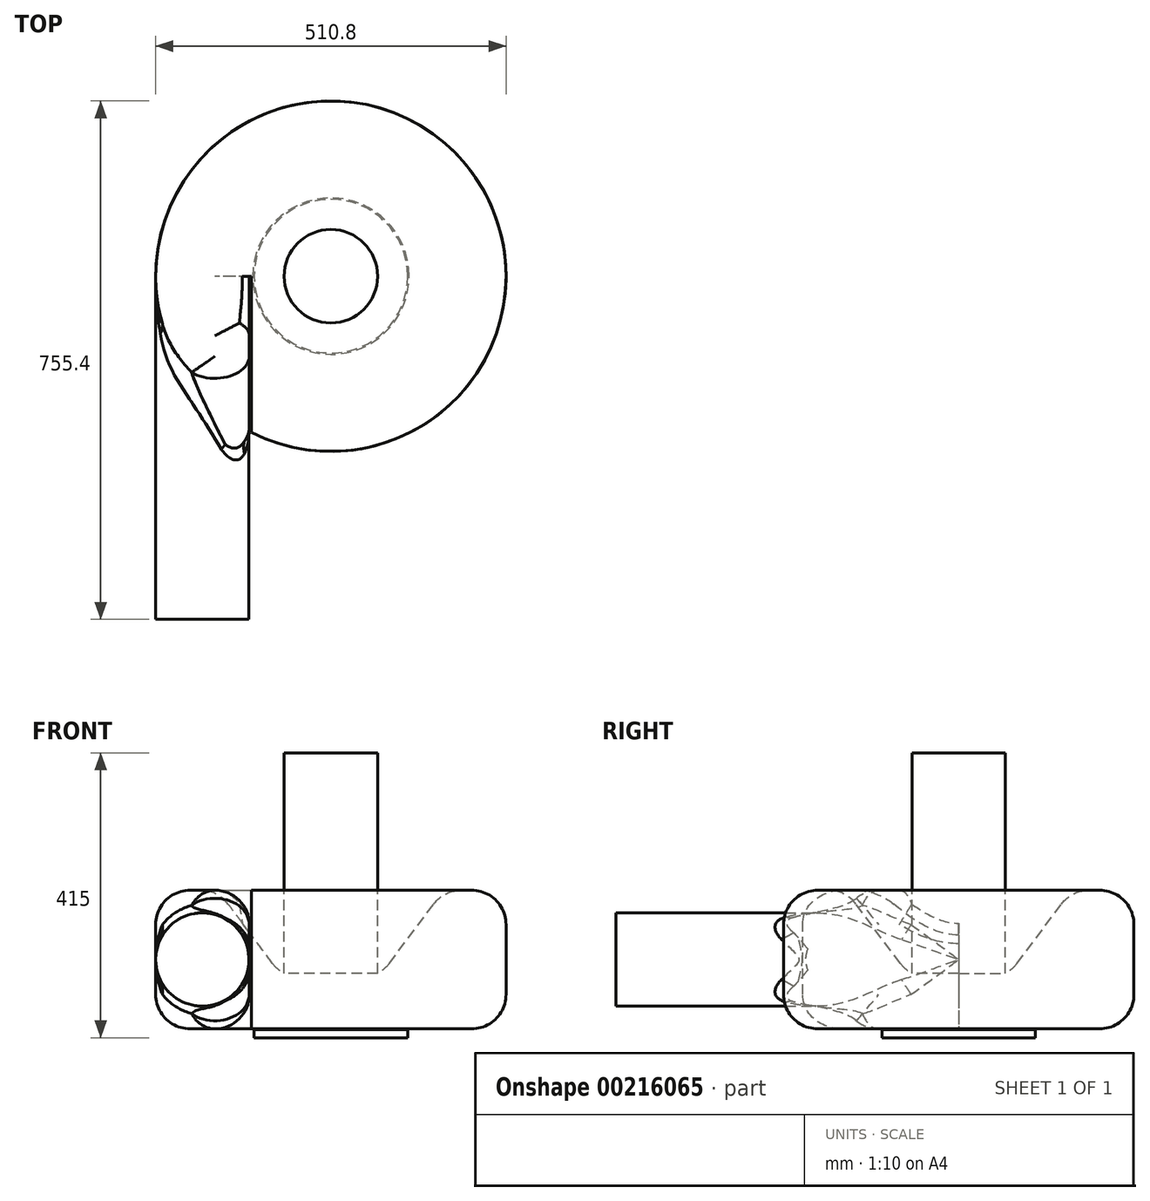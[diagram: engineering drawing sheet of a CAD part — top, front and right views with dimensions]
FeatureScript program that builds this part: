
annotation { "Feature Type Name" : "Feature", "Feature Type Description" : "" }
export const myFeature = defineFeature(function(context is Context, id is Id, definition is map)
    precondition{}
    {
        {
            var Q0;
            Q0=qCreatedBy(makeId("Front.planeOp"),FACE);
            var sketch = newSketch(context, id + "F0", { "sketchPlane" : qUnion([Q0])});
            skLineSegment(sketch, "E0", {"start": v(-114, 169) * mm, "end": v(-255.4, 169) * mm});
            skLineSegment(sketch, "E1", {"start": v(-255.4, 169) * mm, "end": v(-255.4, 371) * mm});
            skLineSegment(sketch, "E2", {"start": v(-255.4, 371) * mm, "end": v(-74.4, 371) * mm});
            skLineSegment(sketch, "E3", {"start": v(-74.4, 371) * mm, "end": v(-74.4, 250) * mm});
            skLineSegment(sketch, "E4", {"start": v(-74.4, 250) * mm, "end": v(-68.2, 250) * mm});
            skLineSegment(sketch, "E5", {"start": v(-68.2, 250) * mm, "end": v(-68.2, 371) * mm});
            skLineSegment(sketch, "E6", {"start": v(-68.2, 371) * mm, "end": v(0, 371) * mm});
            skLineSegment(sketch, "E7", {"start": v(-114, 169) * mm, "end": v(-112, 168) * mm});
            skLineSegment(sketch, "E8", {"start": v(-112, 168) * mm, "end": v(-112, 156) * mm});
            skLineSegment(sketch, "E9", {"start": v(-112, 156) * mm, "end": v(0, 156) * mm});
            skLineSegment(sketch, "E10", {"start": v(0, 371) * mm, "end": v(0, 156) * mm});
            skLineSegment(sketch, "E11", {"start": v(-164.9, 371) * mm, "end": v(-74.4, 250) * mm});
            skSolve(sketch);
        }
        {
            var Q0;
            Q0=makeQuery(id+"F0.imprint","IMPRINT",FACE,{"disambiguationData":[TD([[makeQuery(id+"F0.imprint","IMPRINT",EDGE,{"derivedFrom":sQuery(id+"F0.wireOp",EDGE,"E0")}),-1.0]])]});
            var Q1;
            Q1=sQuery(id+"F0.wireOp",EDGE,"E10");
            revolve(context, id + "F1", {"entities" : qUnion([Q0]), "axis" : qUnion([Q1]), "revolveType" : RevolveType.FULL});
        }
        {
            var Q0;
            Q0=qCreatedBy(makeId("Front.planeOp"),FACE);
            var sketch = newSketch(context, id + "F2", { "sketchPlane" : qUnion([Q0])});
            skCircle(sketch, "E12", {"center": v(-187.4, 270) * mm, "radius": 68 * mm});
            skSolve(sketch);
        }
        {
            var Q0;
            Q0=qSketchRegion(id+"F2",true);
            extrude(context, id + "F3", {"entities" : qUnion([Q0]), "operationType" : NewBodyOperationType.ADD, "depth" : 500 * mm});
        }
        {
            var Q0;
            Q0=makeQuery(id+"F1.opRevolve","SWEPT_FACE",FACE,{"disambiguationData":[OSD([sQuery(id+"F0.wireOp",EDGE,"E6")])]});
            extrude(context, id + "F4", {"entities" : qUnion([Q0]), "operationType" : NewBodyOperationType.ADD, "depth" : 200 * mm});
        }
        {
            var Q0;
            Q0=qCreatedBy(makeId("Top.planeOp"),FACE);
            var sketch = newSketch(context, id + "F5", { "sketchPlane" : qUnion([Q0])});
            skLineSegment(sketch, "E13.bottom", {"start": v(-119, -250) * mm, "end": v(-116, -250) * mm});
            skLineSegment(sketch, "E13.top", {"start": v(-119, 0) * mm, "end": v(-116, 0) * mm});
            skLineSegment(sketch, "E13.left", {"start": v(-119, 0) * mm, "end": v(-119, -250) * mm});
            skLineSegment(sketch, "E13.right", {"start": v(-116, 0) * mm, "end": v(-116, -250) * mm});
            skSolve(sketch);
        }
        {
            var Q0;
            Q0=qSketchRegion(id+"F5",true);
            extrude(context, id + "F6", {"entities" : qUnion([Q0]), "operationType" : NewBodyOperationType.REMOVE, "depth" : 375 * mm});
        }
        {
            var Q0;
            Q0=makeQuery(id+"F1.opRevolve","SWEPT_EDGE",EDGE,{"disambiguationData":[OSD([sQuery(id+"F0.wireOp",EDGE,"E1"),sQuery(id+"F0.wireOp",EDGE,"E2")])]});
            fillet(context, id + "F7", {"entities" : qUnion([Q0]), "radius" : 50 * mm, "tangentPropagation" : true, "allowEdgeOverflow" : false});
        }
        {
            var Q0;
            Q0=makeQuery(id+"F1.opRevolve","SWEPT_EDGE",EDGE,{"disambiguationData":[OSD([sQuery(id+"F0.wireOp",EDGE,"E0"),sQuery(id+"F0.wireOp",EDGE,"E1")])]});
            fillet(context, id + "F8", {"entities" : qUnion([Q0]), "radius" : 50 * mm, "tangentPropagation" : true, "allowEdgeOverflow" : false});
        }
        {
            var Q0;
            Q0=makeQuery(id+"F3.boolean.opBoolean","INTERSECT",EDGE,{"derivedFrom":[makeQuery(id+"F1.opRevolve","SWEPT_FACE",FACE,{"disambiguationData":[OSD([sQuery(id+"F0.wireOp",EDGE,"E1")])]}),makeQuery(id+"F3.opExtrude","SWEPT_FACE",FACE,{"disambiguationData":[OSD([sQuery(id+"F2.wireOp",EDGE,"E12")])]})]});
            var Q1;
            Q1=makeQuery(id+"F3.boolean.opBoolean","INTERSECT",EDGE,{"derivedFrom":[makeQuery(id+"F1.opRevolve","SWEPT_FACE",FACE,{"disambiguationData":[OSD([sQuery(id+"F0.wireOp",EDGE,"E1")])]}),makeQuery(id+"F3.opExtrude","SWEPT_FACE",FACE,{"disambiguationData":[OSD([sQuery(id+"F2.wireOp",EDGE,"E12")])]})]});
            var Q2;
            Q2=makeQuery(id+"F8.opFillet","BLEND_EDGE",EDGE,{"blendedFrom":[makeQuery(id+"F1.opRevolve","SWEPT_EDGE",EDGE,{"disambiguationData":[OSD([sQuery(id+"F0.wireOp",EDGE,"E0"),sQuery(id+"F0.wireOp",EDGE,"E1")])]}),makeQuery(id+"F3.opExtrude","SWEPT_FACE",FACE,{"disambiguationData":[OSD([sQuery(id+"F2.wireOp",EDGE,"E12")])]})],"blendedInto":[makeQuery(id+"F3.opExtrude","SWEPT_FACE",FACE,{"disambiguationData":[OSD([sQuery(id+"F2.wireOp",EDGE,"E12")])]})]});
            var Q3;
            Q3=makeQuery(id+"F3.boolean.opBoolean","INTERSECT",EDGE,{"derivedFrom":[makeQuery(id+"F1.opRevolve","SWEPT_FACE",FACE,{"disambiguationData":[OSD([sQuery(id+"F0.wireOp",EDGE,"E1")])]}),makeQuery(id+"F3.opExtrude","SWEPT_FACE",FACE,{"disambiguationData":[OSD([sQuery(id+"F2.wireOp",EDGE,"E12")])]})]});
            var Q4;
            Q4=makeQuery(id+"F7.opFillet","BLEND_EDGE",EDGE,{"blendedFrom":[makeQuery(id+"F1.opRevolve","SWEPT_EDGE",EDGE,{"disambiguationData":[OSD([sQuery(id+"F0.wireOp",EDGE,"E1"),sQuery(id+"F0.wireOp",EDGE,"E2")])]}),makeQuery(id+"F3.opExtrude","SWEPT_FACE",FACE,{"disambiguationData":[OSD([sQuery(id+"F2.wireOp",EDGE,"E12")])]})],"blendedInto":[makeQuery(id+"F3.opExtrude","SWEPT_FACE",FACE,{"disambiguationData":[OSD([sQuery(id+"F2.wireOp",EDGE,"E12")])]})]});
            fillet(context, id + "F9", {"entities" : qUnion([Q0, Q1, Q2, Q3, Q4]), "radius" : 50 * mm, "tangentPropagation" : true, "allowEdgeOverflow" : false});
        }
        {
            var Q0;
            Q0=makeQuery(id+"F1.opRevolve","SWEPT_EDGE",EDGE,{"disambiguationData":[OSD([sQuery(id+"F0.wireOp",EDGE,"E2"),sQuery(id+"F0.wireOp",EDGE,"E11")])]});
            var Q1;
            Q1=makeQuery(id+"F1.opRevolve","SWEPT_EDGE",EDGE,{"disambiguationData":[OSD([sQuery(id+"F0.wireOp",EDGE,"E3"),sQuery(id+"F0.wireOp",EDGE,"E4"),sQuery(id+"F0.wireOp",EDGE,"E11")])]});
            fillet(context, id + "F10", {"entities" : qUnion([Q0, Q1]), "radius" : 50 * mm, "tangentPropagation" : true, "allowEdgeOverflow" : false});
        }
        {
            var Q0;
            Q0=makeQuery(id+"F6.boolean.opBoolean","INTERSECT",EDGE,{"derivedFrom":[makeQuery(id+"F1.opRevolve","SWEPT_FACE",FACE,{"disambiguationData":[OSD([sQuery(id+"F0.wireOp",EDGE,"E0")])]}),makeQuery(id+"F6.opExtrude","SWEPT_FACE",FACE,{"disambiguationData":[OSD([sQuery(id+"F5.wireOp",EDGE,"E13.left")])]})]});
            var Q1;
            Q1=makeQuery(id+"F8.opFillet","BLEND_EDGE",EDGE,{"blendedFrom":[makeQuery(id+"F1.opRevolve","SWEPT_EDGE",EDGE,{"disambiguationData":[OSD([sQuery(id+"F0.wireOp",EDGE,"E0"),sQuery(id+"F0.wireOp",EDGE,"E1")])]}),makeQuery(id+"F6.boolean.opBoolean","COPY",FACE,{"derivedFrom":makeQuery(id+"F6.opExtrude","SWEPT_FACE",FACE,{"disambiguationData":[OSD([sQuery(id+"F5.wireOp",EDGE,"E13.left")])]})})],"blendedInto":[makeQuery(id+"F6.boolean.opBoolean","COPY",FACE,{"derivedFrom":makeQuery(id+"F6.opExtrude","SWEPT_FACE",FACE,{"disambiguationData":[OSD([sQuery(id+"F5.wireOp",EDGE,"E13.left")])]})})]});
            var Q2;
            Q2=makeQuery(id+"F9.opFillet","BLEND_EDGE",EDGE,{"blendedFrom":[makeQuery(id+"F8.opFillet","BLEND_EDGE",EDGE,{"blendedFrom":[makeQuery(id+"F1.opRevolve","SWEPT_EDGE",EDGE,{"disambiguationData":[OSD([sQuery(id+"F0.wireOp",EDGE,"E0"),sQuery(id+"F0.wireOp",EDGE,"E1")])]}),makeQuery(id+"F3.opExtrude","SWEPT_FACE",FACE,{"disambiguationData":[OSD([sQuery(id+"F2.wireOp",EDGE,"E12")])]})],"blendedInto":[makeQuery(id+"F3.opExtrude","SWEPT_FACE",FACE,{"disambiguationData":[OSD([sQuery(id+"F2.wireOp",EDGE,"E12")])]})]}),makeQuery(id+"F6.boolean.opBoolean","COPY",FACE,{"derivedFrom":makeQuery(id+"F6.opExtrude","SWEPT_FACE",FACE,{"disambiguationData":[OSD([sQuery(id+"F5.wireOp",EDGE,"E13.left")])]})})],"blendedInto":[makeQuery(id+"F6.boolean.opBoolean","COPY",FACE,{"derivedFrom":makeQuery(id+"F6.opExtrude","SWEPT_FACE",FACE,{"disambiguationData":[OSD([sQuery(id+"F5.wireOp",EDGE,"E13.left")])]})})]});
            var Q3;
            Q3=makeQuery(id+"F9.opFillet","BLEND_EDGE",EDGE,{"disambiguationData":[OD(1.0)],"blendedFrom":[makeQuery(id+"F7.opFillet","BLEND_EDGE",EDGE,{"blendedFrom":[makeQuery(id+"F1.opRevolve","SWEPT_EDGE",EDGE,{"disambiguationData":[OSD([sQuery(id+"F0.wireOp",EDGE,"E1"),sQuery(id+"F0.wireOp",EDGE,"E2")])]}),makeQuery(id+"F3.opExtrude","SWEPT_FACE",FACE,{"disambiguationData":[OSD([sQuery(id+"F2.wireOp",EDGE,"E12")])]})],"blendedInto":[makeQuery(id+"F3.opExtrude","SWEPT_FACE",FACE,{"disambiguationData":[OSD([sQuery(id+"F2.wireOp",EDGE,"E12")])]})]}),makeQuery(id+"F6.boolean.opBoolean","COPY",FACE,{"derivedFrom":makeQuery(id+"F6.opExtrude","SWEPT_FACE",FACE,{"disambiguationData":[OSD([sQuery(id+"F5.wireOp",EDGE,"E13.left")])]})})],"blendedInto":[makeQuery(id+"F6.boolean.opBoolean","COPY",FACE,{"derivedFrom":makeQuery(id+"F6.opExtrude","SWEPT_FACE",FACE,{"disambiguationData":[OSD([sQuery(id+"F5.wireOp",EDGE,"E13.left")])]})})]});
            var Q4;
            Q4=makeQuery(id+"F9.opFillet","BLEND_EDGE",EDGE,{"disambiguationData":[OD(0.0)],"blendedFrom":[makeQuery(id+"F7.opFillet","BLEND_EDGE",EDGE,{"blendedFrom":[makeQuery(id+"F1.opRevolve","SWEPT_EDGE",EDGE,{"disambiguationData":[OSD([sQuery(id+"F0.wireOp",EDGE,"E1"),sQuery(id+"F0.wireOp",EDGE,"E2")])]}),makeQuery(id+"F3.opExtrude","SWEPT_FACE",FACE,{"disambiguationData":[OSD([sQuery(id+"F2.wireOp",EDGE,"E12")])]})],"blendedInto":[makeQuery(id+"F3.opExtrude","SWEPT_FACE",FACE,{"disambiguationData":[OSD([sQuery(id+"F2.wireOp",EDGE,"E12")])]})]}),makeQuery(id+"F6.boolean.opBoolean","COPY",FACE,{"derivedFrom":makeQuery(id+"F6.opExtrude","SWEPT_FACE",FACE,{"disambiguationData":[OSD([sQuery(id+"F5.wireOp",EDGE,"E13.left")])]})})],"blendedInto":[makeQuery(id+"F6.boolean.opBoolean","COPY",FACE,{"derivedFrom":makeQuery(id+"F6.opExtrude","SWEPT_FACE",FACE,{"disambiguationData":[OSD([sQuery(id+"F5.wireOp",EDGE,"E13.left")])]})})]});
            var Q5;
            Q5=makeQuery(id+"F7.opFillet","BLEND_EDGE",EDGE,{"blendedFrom":[makeQuery(id+"F1.opRevolve","SWEPT_EDGE",EDGE,{"disambiguationData":[OSD([sQuery(id+"F0.wireOp",EDGE,"E1"),sQuery(id+"F0.wireOp",EDGE,"E2")])]}),makeQuery(id+"F6.boolean.opBoolean","COPY",FACE,{"derivedFrom":makeQuery(id+"F6.opExtrude","SWEPT_FACE",FACE,{"disambiguationData":[OSD([sQuery(id+"F5.wireOp",EDGE,"E13.left")])]})})],"blendedInto":[makeQuery(id+"F6.boolean.opBoolean","COPY",FACE,{"derivedFrom":makeQuery(id+"F6.opExtrude","SWEPT_FACE",FACE,{"disambiguationData":[OSD([sQuery(id+"F5.wireOp",EDGE,"E13.left")])]})})]});
            var Q6;
            Q6=makeQuery(id+"F6.boolean.opBoolean","INTERSECT",EDGE,{"derivedFrom":[makeQuery(id+"F1.opRevolve","SWEPT_FACE",FACE,{"disambiguationData":[OSD([sQuery(id+"F0.wireOp",EDGE,"E2")])]}),makeQuery(id+"F6.opExtrude","SWEPT_FACE",FACE,{"disambiguationData":[OSD([sQuery(id+"F5.wireOp",EDGE,"E13.left")])]})]});
            var Q7;
            Q7=makeQuery(id+"F10.opFillet","BLEND_EDGE",EDGE,{"blendedFrom":[makeQuery(id+"F1.opRevolve","SWEPT_EDGE",EDGE,{"disambiguationData":[OSD([sQuery(id+"F0.wireOp",EDGE,"E2"),sQuery(id+"F0.wireOp",EDGE,"E11")])]}),makeQuery(id+"F6.boolean.opBoolean","COPY",FACE,{"derivedFrom":makeQuery(id+"F6.opExtrude","SWEPT_FACE",FACE,{"disambiguationData":[OSD([sQuery(id+"F5.wireOp",EDGE,"E13.left")])]})})],"blendedInto":[makeQuery(id+"F6.boolean.opBoolean","COPY",FACE,{"derivedFrom":makeQuery(id+"F6.opExtrude","SWEPT_FACE",FACE,{"disambiguationData":[OSD([sQuery(id+"F5.wireOp",EDGE,"E13.left")])]})})]});
            var Q8;
            Q8=makeQuery(id+"F6.boolean.opBoolean","INTERSECT",EDGE,{"derivedFrom":[makeQuery(id+"F1.opRevolve","SWEPT_FACE",FACE,{"disambiguationData":[OSD([sQuery(id+"F0.wireOp",EDGE,"E11")])]}),makeQuery(id+"F6.opExtrude","SWEPT_FACE",FACE,{"disambiguationData":[OSD([sQuery(id+"F5.wireOp",EDGE,"E13.left")])]})]});
            fillet(context, id + "F11", {"entities" : qUnion([Q0, Q1, Q2, Q3, Q4, Q5, Q6, Q7, Q8]), "radius" : 50 * mm, "tangentPropagation" : true, "allowEdgeOverflow" : false});
        }
    });
